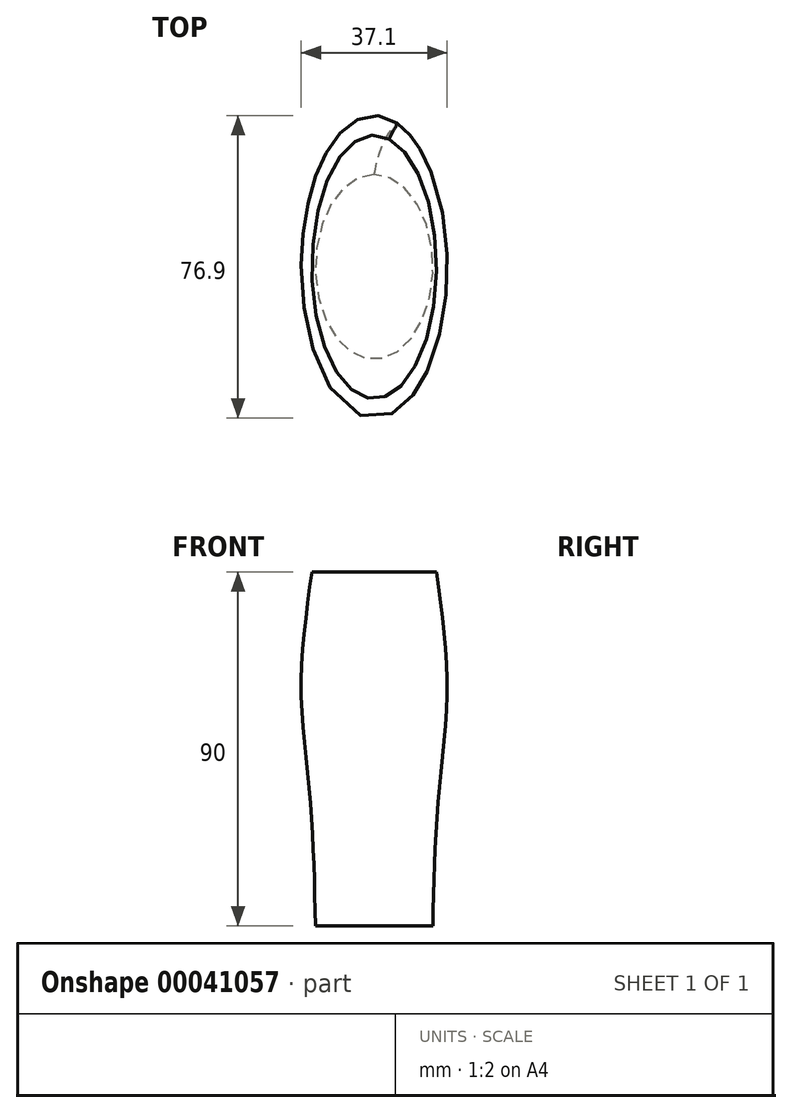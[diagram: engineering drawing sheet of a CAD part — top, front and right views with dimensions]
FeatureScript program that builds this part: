
annotation { "Feature Type Name" : "Feature", "Feature Type Description" : "" }
export const myFeature = defineFeature(function(context is Context, id is Id, definition is map)
    precondition{}
    {
        {
            var Q0;
            Q0=qCreatedBy(makeId("Top.planeOp"),FACE);
            var sketch = newSketch(context, id + "F0", { "sketchPlane" : qUnion([Q0])});
            skEllipse(sketch, "E0", {"center": v(0, 0) * mm, "majorRadius": 23.42 * mm, "minorRadius": 14.92 * mm, "majorAxis": v(0, 1)});
            skSolve(sketch);
        }
        {
            var Q0;
            Q0=qCreatedBy(makeId("Top.planeOp"),FACE);
            cPlane(context, id + "F1", {"entities" : qUnion([Q0]), "cplaneType" : CPlaneType.OFFSET, "offset" : 30 * mm, "width" : 150 * mm, "height" : 150 * mm});
        }
        {
            var Q0;
            Q0=qCreatedBy(id+"F1.planeOp",FACE);
            var sketch = newSketch(context, id + "F2", { "sketchPlane" : qUnion([Q0])});
            skEllipse(sketch, "E1", {"center": v(0, 0) * mm, "majorRadius": 31.83 * mm, "minorRadius": 16.11 * mm, "majorAxis": v(0, 1)});
            skSolve(sketch);
        }
        {
            var Q0;
            Q0=qCreatedBy(id+"F1.planeOp",FACE);
            cPlane(context, id + "F3", {"entities" : qUnion([Q0]), "cplaneType" : CPlaneType.OFFSET, "offset" : 30 * mm, "width" : 150 * mm, "height" : 150 * mm});
        }
        {
            var Q0;
            Q0=qCreatedBy(id+"F3.planeOp",FACE);
            var sketch = newSketch(context, id + "F4", { "sketchPlane" : qUnion([Q0])});
            skEllipse(sketch, "E2", {"center": v(0, 0) * mm, "majorRadius": 38.41 * mm, "minorRadius": 18.54 * mm, "majorAxis": v(0, 1)});
            skSolve(sketch);
        }
        {
            var Q0;
            Q0=qCreatedBy(id+"F3.planeOp",FACE);
            cPlane(context, id + "F5", {"entities" : qUnion([Q0]), "cplaneType" : CPlaneType.OFFSET, "offset" : 30 * mm, "width" : 150 * mm, "height" : 150 * mm});
        }
        {
            var Q0;
            Q0=qCreatedBy(id+"F5.planeOp",FACE);
            var sketch = newSketch(context, id + "F6", { "sketchPlane" : qUnion([Q0])});
            skEllipse(sketch, "E3", {"center": v(0, 0) * mm, "majorRadius": 33.48 * mm, "minorRadius": 15.82 * mm, "majorAxis": v(0, 1)});
            skSolve(sketch);
        }
        {
            var Q0;
            Q0=makeQuery(id+"F0.imprint","IMPRINT",FACE,{"disambiguationData":[TD([[makeQuery(id+"F0.imprint","IMPRINT",EDGE,{"derivedFrom":sQuery(id+"F0.wireOp",EDGE,"E0")}),1.0]])]});
            var Q1;
            Q1=makeQuery(id+"F2.imprint","IMPRINT",FACE,{"disambiguationData":[TD([[makeQuery(id+"F2.imprint","IMPRINT",EDGE,{"derivedFrom":sQuery(id+"F2.wireOp",EDGE,"E1")}),1.0]])]});
            var Q2;
            Q2=makeQuery(id+"F4.imprint","IMPRINT",FACE,{"disambiguationData":[TD([[makeQuery(id+"F4.imprint","IMPRINT",EDGE,{"derivedFrom":sQuery(id+"F4.wireOp",EDGE,"E2")}),1.0]])]});
            var Q3;
            Q3=makeQuery(id+"F6.imprint","IMPRINT",FACE,{"disambiguationData":[TD([[makeQuery(id+"F6.imprint","IMPRINT",EDGE,{"derivedFrom":sQuery(id+"F6.wireOp",EDGE,"E3")}),1.0]])]});
            loft(context, id + "F7", {"sheetProfilesArray" : [{ "sheetProfileEntities" : qUnion([Q0]) }, { "sheetProfileEntities" : qUnion([Q1]) }, { "sheetProfileEntities" : qUnion([Q2]) }, { "sheetProfileEntities" : qUnion([Q3]) }]});
        }
    });
